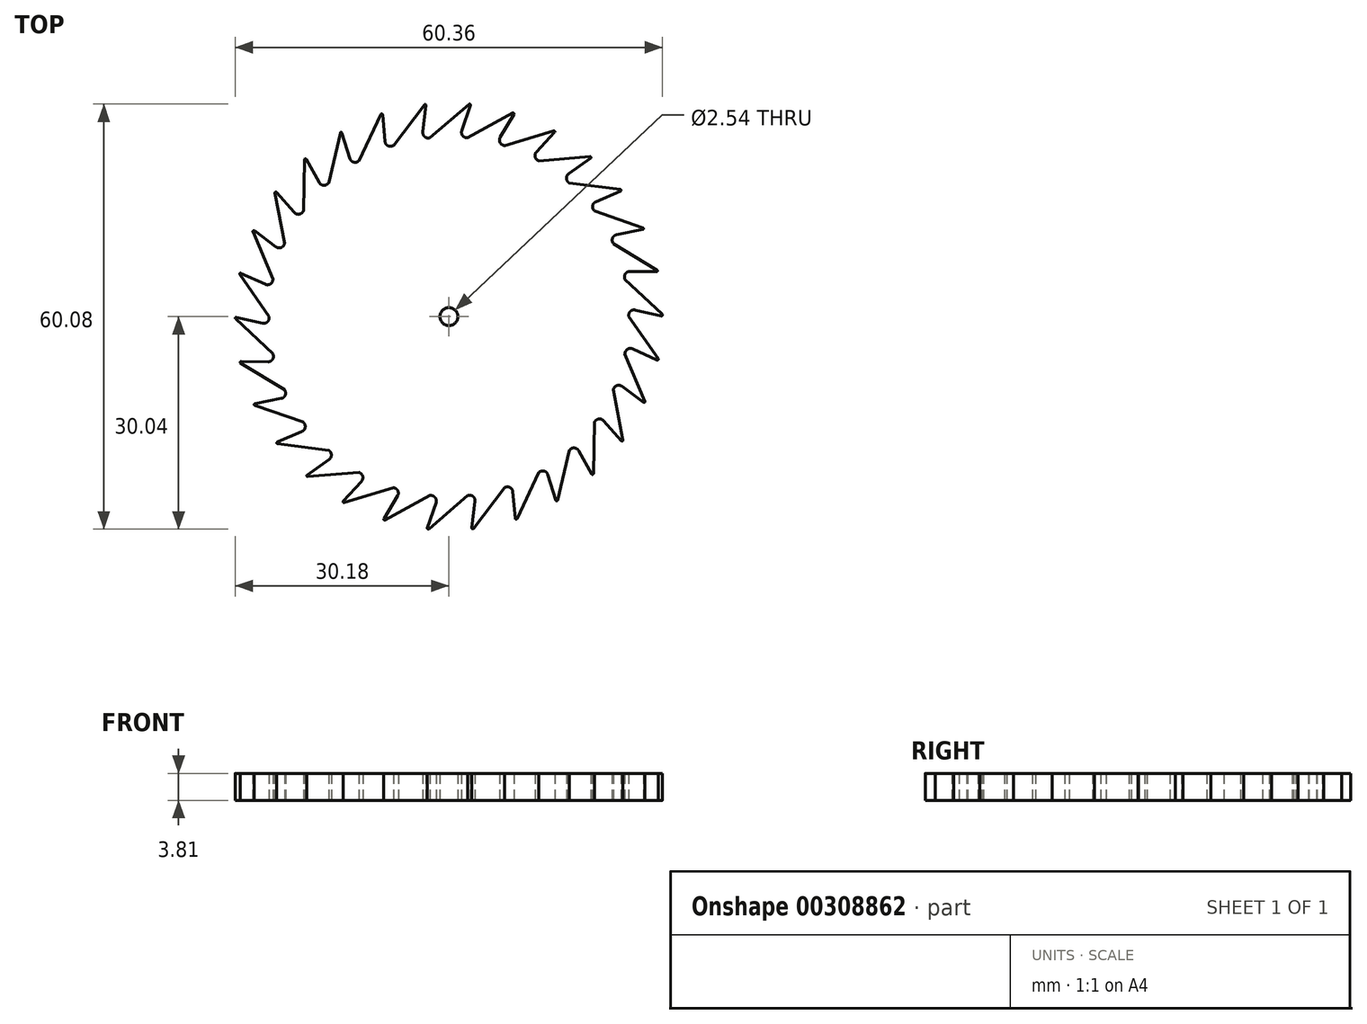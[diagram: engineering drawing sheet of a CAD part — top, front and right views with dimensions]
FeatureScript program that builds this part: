
annotation { "Feature Type Name" : "Feature", "Feature Type Description" : "" }
export const myFeature = defineFeature(function(context is Context, id is Id, definition is map)
    precondition{}
    {
        {
            var Q0;
            Q0=qCreatedBy(makeId("Top.planeOp"),FACE);
            var sketch = newSketch(context, id + "F0", { "sketchPlane" : qUnion([Q0])});
            skCircle(sketch, "E0", {"center": v(0, 0) * mm, "radius": 30.48 * mm, "construction": true});
            skCircle(sketch, "E1", {"center": v(0, 0) * mm, "radius": 25.4 * mm, "construction": true});
            skLineSegment(sketch, "E2", {"start": v(0, 0) * mm, "end": v(4.4, 41.84) * mm, "construction": true});
            skLineSegment(sketch, "E3", {"start": v(0, 0) * mm, "end": v(-4.35, 41.4) * mm, "construction": true});
            skLineSegment(sketch, "E4", {"start": v(0, 0) * mm, "end": v(0, 41.14) * mm, "construction": true});
            skLineSegment(sketch, "E5", {"start": v(2.83, 30) * mm, "end": v(-2.66, 25.26) * mm});
            skLineSegment(sketch, "E6", {"start": v(3.04, 29.87) * mm, "end": v(1.82, 26.28) * mm});
            skArc(sketch, "E7", {"start": v(2.66, 25.26) * mm, "mid": v(2.56, 25.27) * mm, "end": v(2.47, 25.28) * mm});
            skPoint(sketch, "E8.visualSharp", {"position": v(1.5, 25.36) * mm});
            skArc(sketch, "E8.filletArc", {"start": v(1.82, 26.28) * mm, "mid": v(1.9, 25.62) * mm, "end": v(2.47, 25.28) * mm});
            skPoint(sketch, "E9.visualSharp", {"position": v(3.19, 30.31) * mm});
            skArc(sketch, "E9.filletArc", {"start": v(3.04, 29.87) * mm, "mid": v(2.99, 30.02) * mm, "end": v(2.83, 30) * mm});
            skLineSegment(sketch, "E10.1.0", {"start": v(-3.47, 29.94) * mm, "end": v(-7.85, 24.16) * mm});
            skArc(sketch, "E10.1.1", {"start": v(-3.24, 29.85) * mm, "mid": v(-3.32, 29.98) * mm, "end": v(-3.47, 29.94) * mm});
            skLineSegment(sketch, "E10.1.2", {"start": v(-3.24, 29.85) * mm, "end": v(-3.68, 26.09) * mm});
            skArc(sketch, "E10.1.3", {"start": v(-3.68, 26.09) * mm, "mid": v(-3.46, 25.46) * mm, "end": v(-2.84, 25.24) * mm});
            skArc(sketch, "E10.1.4", {"start": v(-2.66, 25.26) * mm, "mid": v(-2.75, 25.25) * mm, "end": v(-2.84, 25.24) * mm});
            skLineSegment(sketch, "E10.2.0", {"start": v(-9.62, 28.57) * mm, "end": v(-12.7, 22) * mm});
            skArc(sketch, "E10.2.1", {"start": v(-9.38, 28.52) * mm, "mid": v(-9.48, 28.64) * mm, "end": v(-9.62, 28.57) * mm});
            skLineSegment(sketch, "E10.2.2", {"start": v(-9.38, 28.52) * mm, "end": v(-9.02, 24.75) * mm});
            skArc(sketch, "E10.2.3", {"start": v(-9.02, 24.75) * mm, "mid": v(-8.68, 24.18) * mm, "end": v(-8.03, 24.1) * mm});
            skArc(sketch, "E10.2.4", {"start": v(-7.85, 24.16) * mm, "mid": v(-7.94, 24.13) * mm, "end": v(-8.03, 24.1) * mm});
            skLineSegment(sketch, "E10.3.0", {"start": v(-15.35, 25.94) * mm, "end": v(-17, 18.88) * mm});
            skArc(sketch, "E10.3.1", {"start": v(-15.1, 25.95) * mm, "mid": v(-15.23, 26.04) * mm, "end": v(-15.35, 25.94) * mm});
            skLineSegment(sketch, "E10.3.2", {"start": v(-15.1, 25.95) * mm, "end": v(-13.97, 22.33) * mm});
            skArc(sketch, "E10.3.3", {"start": v(-13.97, 22.33) * mm, "mid": v(-13.52, 21.85) * mm, "end": v(-12.86, 21.9) * mm});
            skArc(sketch, "E10.3.4", {"start": v(-12.7, 22) * mm, "mid": v(-12.78, 21.95) * mm, "end": v(-12.86, 21.9) * mm});
            skLineSegment(sketch, "E10.4.0", {"start": v(-20.4, 22.18) * mm, "end": v(-20.55, 14.93) * mm});
            skArc(sketch, "E10.4.1", {"start": v(-20.17, 22.24) * mm, "mid": v(-20.3, 22.3) * mm, "end": v(-20.4, 22.18) * mm});
            skLineSegment(sketch, "E10.4.2", {"start": v(-20.17, 22.24) * mm, "end": v(-18.31, 18.94) * mm});
            skArc(sketch, "E10.4.3", {"start": v(-18.31, 18.94) * mm, "mid": v(-17.77, 18.56) * mm, "end": v(-17.13, 18.75) * mm});
            skArc(sketch, "E10.4.4", {"start": v(-17, 18.88) * mm, "mid": v(-17.06, 18.81) * mm, "end": v(-17.13, 18.75) * mm});
            skLineSegment(sketch, "E10.5.0", {"start": v(-24.57, 17.46) * mm, "end": v(-23.2, 10.33) * mm});
            skArc(sketch, "E10.5.1", {"start": v(-24.35, 17.57) * mm, "mid": v(-24.5, 17.6) * mm, "end": v(-24.57, 17.46) * mm});
            skLineSegment(sketch, "E10.5.2", {"start": v(-24.35, 17.57) * mm, "end": v(-21.85, 14.72) * mm});
            skArc(sketch, "E10.5.3", {"start": v(-21.85, 14.72) * mm, "mid": v(-21.24, 14.46) * mm, "end": v(-20.66, 14.78) * mm});
            skArc(sketch, "E10.5.4", {"start": v(-20.55, 14.93) * mm, "mid": v(-20.6, 14.85) * mm, "end": v(-20.66, 14.78) * mm});
            skLineSegment(sketch, "E10.6.0", {"start": v(-27.66, 11.97) * mm, "end": v(-24.84, 5.28) * mm});
            skArc(sketch, "E10.6.1", {"start": v(-27.47, 12.12) * mm, "mid": v(-27.62, 12.12) * mm, "end": v(-27.66, 11.97) * mm});
            skLineSegment(sketch, "E10.6.2", {"start": v(-27.47, 12.12) * mm, "end": v(-24.43, 9.85) * mm});
            skArc(sketch, "E10.6.3", {"start": v(-24.43, 9.85) * mm, "mid": v(-23.78, 9.73) * mm, "end": v(-23.28, 10.16) * mm});
            skArc(sketch, "E10.6.4", {"start": v(-23.2, 10.33) * mm, "mid": v(-23.24, 10.25) * mm, "end": v(-23.28, 10.16) * mm});
            skLineSegment(sketch, "E10.7.0", {"start": v(-29.55, 5.95) * mm, "end": v(-25.4, 0) * mm});
            skArc(sketch, "E10.7.1", {"start": v(-29.4, 6.14) * mm, "mid": v(-29.54, 6.1) * mm, "end": v(-29.55, 5.95) * mm});
            skLineSegment(sketch, "E10.7.2", {"start": v(-29.4, 6.14) * mm, "end": v(-25.95, 4.56) * mm});
            skArc(sketch, "E10.7.3", {"start": v(-25.95, 4.56) * mm, "mid": v(-25.29, 4.57) * mm, "end": v(-24.88, 5.1) * mm});
            skArc(sketch, "E10.7.4", {"start": v(-24.84, 5.28) * mm, "mid": v(-24.86, 5.2) * mm, "end": v(-24.88, 5.1) * mm});
            skLineSegment(sketch, "E10.8.0", {"start": v(-30.14, -0.32) * mm, "end": v(-24.84, -5.28) * mm});
            skArc(sketch, "E10.8.1", {"start": v(-30.02, -0.1) * mm, "mid": v(-30.16, -0.17) * mm, "end": v(-30.14, -0.32) * mm});
            skLineSegment(sketch, "E10.8.2", {"start": v(-30.02, -0.1) * mm, "end": v(-26.33, -0.93) * mm});
            skArc(sketch, "E10.8.3", {"start": v(-26.33, -0.93) * mm, "mid": v(-25.68, -0.78) * mm, "end": v(-25.4, -0.19) * mm});
            skArc(sketch, "E10.8.4", {"start": v(-25.4, 0) * mm, "mid": v(-25.4, -0.1) * mm, "end": v(-25.4, -0.19) * mm});
            skLineSegment(sketch, "E10.9.0", {"start": v(-29.41, -6.58) * mm, "end": v(-23.2, -10.33) * mm});
            skArc(sketch, "E10.9.1", {"start": v(-29.35, -6.34) * mm, "mid": v(-29.47, -6.43) * mm, "end": v(-29.41, -6.58) * mm});
            skLineSegment(sketch, "E10.9.2", {"start": v(-29.35, -6.34) * mm, "end": v(-25.56, -6.39) * mm});
            skArc(sketch, "E10.9.3", {"start": v(-25.56, -6.39) * mm, "mid": v(-24.96, -6.1) * mm, "end": v(-24.8, -5.46) * mm});
            skArc(sketch, "E10.9.4", {"start": v(-24.84, -5.28) * mm, "mid": v(-24.83, -5.37) * mm, "end": v(-24.8, -5.46) * mm});
            skLineSegment(sketch, "E10.10.0", {"start": v(-27.4, -12.55) * mm, "end": v(-20.55, -14.93) * mm});
            skArc(sketch, "E10.10.1", {"start": v(-27.39, -12.3) * mm, "mid": v(-27.49, -12.42) * mm, "end": v(-27.4, -12.55) * mm});
            skLineSegment(sketch, "E10.10.2", {"start": v(-27.39, -12.3) * mm, "end": v(-23.67, -11.56) * mm});
            skArc(sketch, "E10.10.3", {"start": v(-23.67, -11.56) * mm, "mid": v(-23.14, -11.16) * mm, "end": v(-23.13, -10.5) * mm});
            skArc(sketch, "E10.10.4", {"start": v(-23.2, -10.33) * mm, "mid": v(-23.17, -10.42) * mm, "end": v(-23.13, -10.5) * mm});
            skLineSegment(sketch, "E10.11.0", {"start": v(-24.2, -17.97) * mm, "end": v(-17, -18.88) * mm});
            skArc(sketch, "E10.11.1", {"start": v(-24.23, -17.73) * mm, "mid": v(-24.3, -17.87) * mm, "end": v(-24.2, -17.97) * mm});
            skLineSegment(sketch, "E10.11.2", {"start": v(-24.23, -17.73) * mm, "end": v(-20.75, -16.23) * mm});
            skArc(sketch, "E10.11.3", {"start": v(-20.75, -16.23) * mm, "mid": v(-20.32, -15.73) * mm, "end": v(-20.44, -15.08) * mm});
            skArc(sketch, "E10.11.4", {"start": v(-20.55, -14.93) * mm, "mid": v(-20.5, -15) * mm, "end": v(-20.44, -15.08) * mm});
            skLineSegment(sketch, "E10.12.0", {"start": v(-19.93, -22.61) * mm, "end": v(-12.7, -22) * mm});
            skArc(sketch, "E10.12.1", {"start": v(-20.01, -22.38) * mm, "mid": v(-20.06, -22.53) * mm, "end": v(-19.93, -22.61) * mm});
            skLineSegment(sketch, "E10.12.2", {"start": v(-20.01, -22.38) * mm, "end": v(-16.92, -20.2) * mm});
            skArc(sketch, "E10.12.3", {"start": v(-16.92, -20.2) * mm, "mid": v(-16.6, -19.61) * mm, "end": v(-16.86, -19) * mm});
            skArc(sketch, "E10.12.4", {"start": v(-17, -18.88) * mm, "mid": v(-16.93, -18.94) * mm, "end": v(-16.86, -19) * mm});
            skLineSegment(sketch, "E10.13.0", {"start": v(-14.8, -26.26) * mm, "end": v(-7.85, -24.16) * mm});
            skArc(sketch, "E10.13.1", {"start": v(-14.92, -26.05) * mm, "mid": v(-14.94, -26.2) * mm, "end": v(-14.8, -26.26) * mm});
            skLineSegment(sketch, "E10.13.2", {"start": v(-14.92, -26.05) * mm, "end": v(-12.35, -23.27) * mm});
            skArc(sketch, "E10.13.3", {"start": v(-12.35, -23.27) * mm, "mid": v(-12.16, -22.63) * mm, "end": v(-12.54, -22.09) * mm});
            skArc(sketch, "E10.13.4", {"start": v(-12.7, -22) * mm, "mid": v(-12.62, -22.04) * mm, "end": v(-12.54, -22.09) * mm});
            skLineSegment(sketch, "E10.14.0", {"start": v(-9.01, -28.76) * mm, "end": v(-2.66, -25.26) * mm});
            skArc(sketch, "E10.14.1", {"start": v(-9.18, -28.59) * mm, "mid": v(-9.16, -28.74) * mm, "end": v(-9.01, -28.76) * mm});
            skLineSegment(sketch, "E10.14.2", {"start": v(-9.18, -28.59) * mm, "end": v(-7.25, -25.33) * mm});
            skArc(sketch, "E10.14.3", {"start": v(-7.25, -25.33) * mm, "mid": v(-7.2, -24.67) * mm, "end": v(-7.67, -24.21) * mm});
            skArc(sketch, "E10.14.4", {"start": v(-7.85, -24.16) * mm, "mid": v(-7.76, -24.19) * mm, "end": v(-7.67, -24.21) * mm});
            skLineSegment(sketch, "E10.15.0", {"start": v(-2.83, -30) * mm, "end": v(2.66, -25.26) * mm});
            skArc(sketch, "E10.15.1", {"start": v(-3.04, -29.87) * mm, "mid": v(-2.99, -30.02) * mm, "end": v(-2.83, -30) * mm});
            skLineSegment(sketch, "E10.15.2", {"start": v(-3.04, -29.87) * mm, "end": v(-1.82, -26.28) * mm});
            skArc(sketch, "E10.15.3", {"start": v(-1.82, -26.28) * mm, "mid": v(-1.9, -25.62) * mm, "end": v(-2.47, -25.28) * mm});
            skArc(sketch, "E10.15.4", {"start": v(-2.66, -25.26) * mm, "mid": v(-2.56, -25.27) * mm, "end": v(-2.47, -25.28) * mm});
            skLineSegment(sketch, "E10.16.0", {"start": v(3.47, -29.94) * mm, "end": v(7.85, -24.16) * mm});
            skArc(sketch, "E10.16.1", {"start": v(3.24, -29.85) * mm, "mid": v(3.32, -29.98) * mm, "end": v(3.47, -29.94) * mm});
            skLineSegment(sketch, "E10.16.2", {"start": v(3.24, -29.85) * mm, "end": v(3.68, -26.09) * mm});
            skArc(sketch, "E10.16.3", {"start": v(3.68, -26.09) * mm, "mid": v(3.46, -25.46) * mm, "end": v(2.84, -25.24) * mm});
            skArc(sketch, "E10.16.4", {"start": v(2.66, -25.26) * mm, "mid": v(2.75, -25.25) * mm, "end": v(2.84, -25.24) * mm});
            skLineSegment(sketch, "E10.17.0", {"start": v(9.62, -28.57) * mm, "end": v(12.7, -22) * mm});
            skArc(sketch, "E10.17.1", {"start": v(9.38, -28.52) * mm, "mid": v(9.48, -28.64) * mm, "end": v(9.62, -28.57) * mm});
            skLineSegment(sketch, "E10.17.2", {"start": v(9.38, -28.52) * mm, "end": v(9.02, -24.75) * mm});
            skArc(sketch, "E10.17.3", {"start": v(9.02, -24.75) * mm, "mid": v(8.68, -24.18) * mm, "end": v(8.03, -24.1) * mm});
            skArc(sketch, "E10.17.4", {"start": v(7.85, -24.16) * mm, "mid": v(7.94, -24.13) * mm, "end": v(8.03, -24.1) * mm});
            skLineSegment(sketch, "E10.18.0", {"start": v(15.35, -25.94) * mm, "end": v(17, -18.88) * mm});
            skArc(sketch, "E10.18.1", {"start": v(15.1, -25.95) * mm, "mid": v(15.23, -26.04) * mm, "end": v(15.35, -25.94) * mm});
            skLineSegment(sketch, "E10.18.2", {"start": v(15.1, -25.95) * mm, "end": v(13.97, -22.33) * mm});
            skArc(sketch, "E10.18.3", {"start": v(13.97, -22.33) * mm, "mid": v(13.52, -21.85) * mm, "end": v(12.86, -21.9) * mm});
            skArc(sketch, "E10.18.4", {"start": v(12.7, -22) * mm, "mid": v(12.78, -21.95) * mm, "end": v(12.86, -21.9) * mm});
            skLineSegment(sketch, "E10.19.0", {"start": v(20.4, -22.18) * mm, "end": v(20.55, -14.93) * mm});
            skArc(sketch, "E10.19.1", {"start": v(20.17, -22.24) * mm, "mid": v(20.3, -22.3) * mm, "end": v(20.4, -22.18) * mm});
            skLineSegment(sketch, "E10.19.2", {"start": v(20.17, -22.24) * mm, "end": v(18.31, -18.94) * mm});
            skArc(sketch, "E10.19.3", {"start": v(18.31, -18.94) * mm, "mid": v(17.77, -18.56) * mm, "end": v(17.13, -18.75) * mm});
            skArc(sketch, "E10.19.4", {"start": v(17, -18.88) * mm, "mid": v(17.06, -18.81) * mm, "end": v(17.13, -18.75) * mm});
            skLineSegment(sketch, "E10.20.0", {"start": v(24.57, -17.46) * mm, "end": v(23.2, -10.33) * mm});
            skArc(sketch, "E10.20.1", {"start": v(24.35, -17.57) * mm, "mid": v(24.5, -17.6) * mm, "end": v(24.57, -17.46) * mm});
            skLineSegment(sketch, "E10.20.2", {"start": v(24.35, -17.57) * mm, "end": v(21.85, -14.72) * mm});
            skArc(sketch, "E10.20.3", {"start": v(21.85, -14.72) * mm, "mid": v(21.24, -14.46) * mm, "end": v(20.66, -14.78) * mm});
            skArc(sketch, "E10.20.4", {"start": v(20.55, -14.93) * mm, "mid": v(20.6, -14.85) * mm, "end": v(20.66, -14.78) * mm});
            skLineSegment(sketch, "E10.21.0", {"start": v(27.66, -11.97) * mm, "end": v(24.84, -5.28) * mm});
            skArc(sketch, "E10.21.1", {"start": v(27.47, -12.12) * mm, "mid": v(27.62, -12.12) * mm, "end": v(27.66, -11.97) * mm});
            skLineSegment(sketch, "E10.21.2", {"start": v(27.47, -12.12) * mm, "end": v(24.43, -9.85) * mm});
            skArc(sketch, "E10.21.3", {"start": v(24.43, -9.85) * mm, "mid": v(23.78, -9.73) * mm, "end": v(23.28, -10.16) * mm});
            skArc(sketch, "E10.21.4", {"start": v(23.2, -10.33) * mm, "mid": v(23.24, -10.25) * mm, "end": v(23.28, -10.16) * mm});
            skLineSegment(sketch, "E10.22.0", {"start": v(29.55, -5.95) * mm, "end": v(25.4, 0) * mm});
            skArc(sketch, "E10.22.1", {"start": v(29.4, -6.14) * mm, "mid": v(29.54, -6.1) * mm, "end": v(29.55, -5.95) * mm});
            skLineSegment(sketch, "E10.22.2", {"start": v(29.4, -6.14) * mm, "end": v(25.95, -4.56) * mm});
            skArc(sketch, "E10.22.3", {"start": v(25.95, -4.56) * mm, "mid": v(25.29, -4.57) * mm, "end": v(24.88, -5.1) * mm});
            skArc(sketch, "E10.22.4", {"start": v(24.84, -5.28) * mm, "mid": v(24.86, -5.2) * mm, "end": v(24.88, -5.1) * mm});
            skLineSegment(sketch, "E10.23.0", {"start": v(30.14, 0.32) * mm, "end": v(24.84, 5.28) * mm});
            skArc(sketch, "E10.23.1", {"start": v(30.02, 0.1) * mm, "mid": v(30.16, 0.17) * mm, "end": v(30.14, 0.32) * mm});
            skLineSegment(sketch, "E10.23.2", {"start": v(30.02, 0.1) * mm, "end": v(26.33, 0.93) * mm});
            skArc(sketch, "E10.23.3", {"start": v(26.33, 0.93) * mm, "mid": v(25.68, 0.78) * mm, "end": v(25.4, 0.19) * mm});
            skArc(sketch, "E10.23.4", {"start": v(25.4, 0) * mm, "mid": v(25.4, 0.1) * mm, "end": v(25.4, 0.19) * mm});
            skLineSegment(sketch, "E10.24.0", {"start": v(29.41, 6.58) * mm, "end": v(23.2, 10.33) * mm});
            skArc(sketch, "E10.24.1", {"start": v(29.35, 6.34) * mm, "mid": v(29.47, 6.43) * mm, "end": v(29.41, 6.58) * mm});
            skLineSegment(sketch, "E10.24.2", {"start": v(29.35, 6.34) * mm, "end": v(25.56, 6.39) * mm});
            skArc(sketch, "E10.24.3", {"start": v(25.56, 6.39) * mm, "mid": v(24.96, 6.1) * mm, "end": v(24.8, 5.46) * mm});
            skArc(sketch, "E10.24.4", {"start": v(24.84, 5.28) * mm, "mid": v(24.83, 5.37) * mm, "end": v(24.8, 5.46) * mm});
            skLineSegment(sketch, "E10.25.0", {"start": v(27.4, 12.55) * mm, "end": v(20.55, 14.93) * mm});
            skArc(sketch, "E10.25.1", {"start": v(27.39, 12.3) * mm, "mid": v(27.49, 12.42) * mm, "end": v(27.4, 12.55) * mm});
            skLineSegment(sketch, "E10.25.2", {"start": v(27.39, 12.3) * mm, "end": v(23.67, 11.56) * mm});
            skArc(sketch, "E10.25.3", {"start": v(23.67, 11.56) * mm, "mid": v(23.14, 11.16) * mm, "end": v(23.13, 10.5) * mm});
            skArc(sketch, "E10.25.4", {"start": v(23.2, 10.33) * mm, "mid": v(23.17, 10.42) * mm, "end": v(23.13, 10.5) * mm});
            skLineSegment(sketch, "E10.26.0", {"start": v(24.2, 17.97) * mm, "end": v(17, 18.88) * mm});
            skArc(sketch, "E10.26.1", {"start": v(24.23, 17.73) * mm, "mid": v(24.3, 17.87) * mm, "end": v(24.2, 17.97) * mm});
            skLineSegment(sketch, "E10.26.2", {"start": v(24.23, 17.73) * mm, "end": v(20.75, 16.23) * mm});
            skArc(sketch, "E10.26.3", {"start": v(20.75, 16.23) * mm, "mid": v(20.32, 15.73) * mm, "end": v(20.44, 15.08) * mm});
            skArc(sketch, "E10.26.4", {"start": v(20.55, 14.93) * mm, "mid": v(20.5, 15) * mm, "end": v(20.44, 15.08) * mm});
            skLineSegment(sketch, "E10.27.0", {"start": v(19.93, 22.61) * mm, "end": v(12.7, 22) * mm});
            skArc(sketch, "E10.27.1", {"start": v(20.01, 22.38) * mm, "mid": v(20.06, 22.53) * mm, "end": v(19.93, 22.61) * mm});
            skLineSegment(sketch, "E10.27.2", {"start": v(20.01, 22.38) * mm, "end": v(16.92, 20.2) * mm});
            skArc(sketch, "E10.27.3", {"start": v(16.92, 20.2) * mm, "mid": v(16.6, 19.61) * mm, "end": v(16.86, 19) * mm});
            skArc(sketch, "E10.27.4", {"start": v(17, 18.88) * mm, "mid": v(16.93, 18.94) * mm, "end": v(16.86, 19) * mm});
            skLineSegment(sketch, "E10.28.0", {"start": v(14.8, 26.26) * mm, "end": v(7.85, 24.16) * mm});
            skArc(sketch, "E10.28.1", {"start": v(14.92, 26.05) * mm, "mid": v(14.94, 26.2) * mm, "end": v(14.8, 26.26) * mm});
            skLineSegment(sketch, "E10.28.2", {"start": v(14.92, 26.05) * mm, "end": v(12.35, 23.27) * mm});
            skArc(sketch, "E10.28.3", {"start": v(12.35, 23.27) * mm, "mid": v(12.16, 22.63) * mm, "end": v(12.54, 22.09) * mm});
            skArc(sketch, "E10.28.4", {"start": v(12.7, 22) * mm, "mid": v(12.62, 22.04) * mm, "end": v(12.54, 22.09) * mm});
            skLineSegment(sketch, "E10.29.0", {"start": v(9.01, 28.76) * mm, "end": v(2.66, 25.26) * mm});
            skArc(sketch, "E10.29.1", {"start": v(9.18, 28.59) * mm, "mid": v(9.16, 28.74) * mm, "end": v(9.01, 28.76) * mm});
            skLineSegment(sketch, "E10.29.2", {"start": v(9.18, 28.59) * mm, "end": v(7.25, 25.33) * mm});
            skArc(sketch, "E10.29.3", {"start": v(7.25, 25.33) * mm, "mid": v(7.2, 24.67) * mm, "end": v(7.67, 24.21) * mm});
            skArc(sketch, "E10.29.4", {"start": v(7.85, 24.16) * mm, "mid": v(7.76, 24.19) * mm, "end": v(7.67, 24.21) * mm});
            skCircle(sketch, "E11", {"center": v(0, 0) * mm, "radius": 1.27 * mm});
            skSolve(sketch);
        }
        {
            var Q0;
            Q0 = qSketchRegion(id + "F0", true);
            extrude(context, id + "F1", {"entities" : qUnion([Q0]), "depth" : 3.8 * mm});
        }
    });
